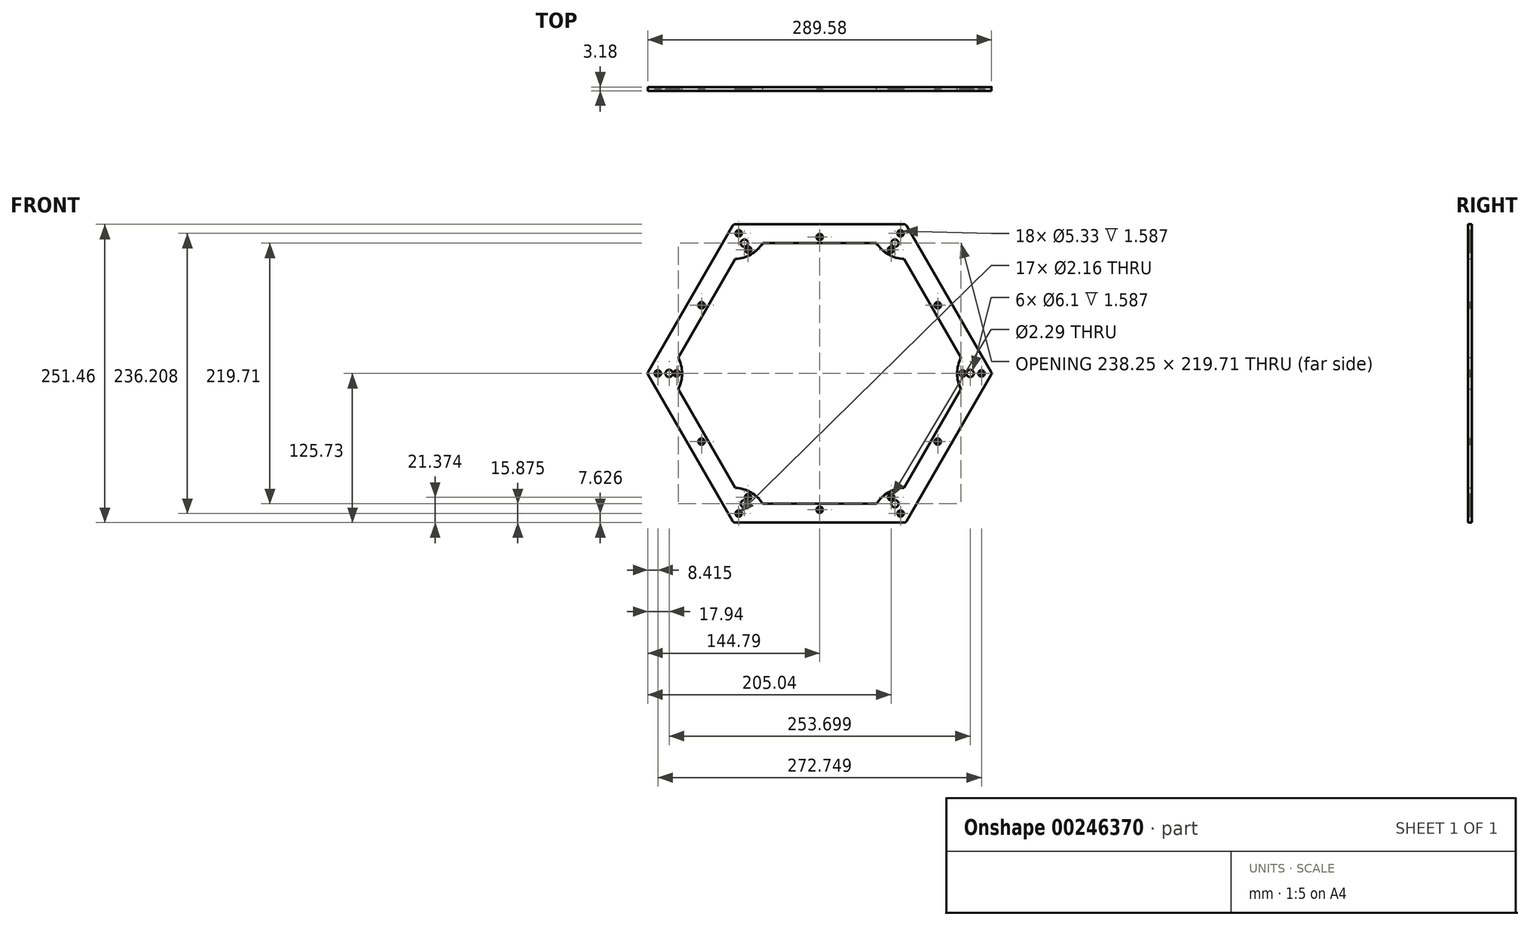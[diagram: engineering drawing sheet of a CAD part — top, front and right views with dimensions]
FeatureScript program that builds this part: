
annotation { "Feature Type Name" : "Feature", "Feature Type Description" : "" }
export const myFeature = defineFeature(function(context is Context, id is Id, definition is map)
    precondition{}
    {
        {
            var Q0;
            Q0=qCreatedBy(makeId("Front.planeOp"),FACE);
            var sketch = newSketch(context, id + "F0", { "sketchPlane" : qUnion([Q0])});
            skCircle(sketch, "E0.cCircle", {"center": v(0, 0) * mm, "radius": 125.73 * mm, "construction": true});
            skLineSegment(sketch, "E0.0", {"start": v(-72.6, 125.73) * mm, "end": v(72.6, 125.73) * mm});
            skLineSegment(sketch, "E0.1", {"start": v(72.6, 125.73) * mm, "end": v(145.18, 0) * mm});
            skLineSegment(sketch, "E0.2", {"start": v(145.18, 0) * mm, "end": v(72.6, -125.73) * mm});
            skLineSegment(sketch, "E0.3", {"start": v(72.6, -125.73) * mm, "end": v(-72.6, -125.73) * mm});
            skLineSegment(sketch, "E0.4", {"start": v(-72.6, -125.73) * mm, "end": v(-145.18, 0) * mm});
            skLineSegment(sketch, "E0.5", {"start": v(-145.18, 0) * mm, "end": v(-72.6, 125.73) * mm});
            skPoint(sketch, "E0.0.midPoint", {"position": v(0, 125.73) * mm});
            skLineSegment(sketch, "E1", {"start": v(0, 0) * mm, "end": v(-103.66, 179.55) * mm, "construction": true});
            skLineSegment(sketch, "E2", {"start": v(0, 0) * mm, "end": v(108.03, 187.1) * mm, "construction": true});
            skLineSegment(sketch, "E3", {"start": v(0, 0) * mm, "end": v(215.11, 0) * mm, "construction": true});
            skLineSegment(sketch, "E4", {"start": v(0, 0) * mm, "end": v(129.36, -224.05) * mm, "construction": true});
            skLineSegment(sketch, "E5", {"start": v(0, 0) * mm, "end": v(-137.05, -237.38) * mm, "construction": true});
            skLineSegment(sketch, "E6", {"start": v(0, 0) * mm, "end": v(-290.92, 0) * mm, "construction": true});
            skCircle(sketch, "E7.cCircle", {"center": v(0, 0) * mm, "radius": 109.86 * mm, "construction": true});
            skLineSegment(sketch, "E7.0", {"start": v(-63.42, 109.86) * mm, "end": v(63.42, 109.86) * mm});
            skLineSegment(sketch, "E7.1", {"start": v(63.42, 109.85) * mm, "end": v(126.85, 0) * mm});
            skLineSegment(sketch, "E7.2", {"start": v(126.85, 0) * mm, "end": v(63.42, -109.86) * mm});
            skLineSegment(sketch, "E7.3", {"start": v(63.42, -109.85) * mm, "end": v(-63.42, -109.86) * mm});
            skLineSegment(sketch, "E7.4", {"start": v(-63.42, -109.86) * mm, "end": v(-126.85, 0) * mm});
            skLineSegment(sketch, "E7.5", {"start": v(-126.85, 0) * mm, "end": v(-63.42, 109.86) * mm});
            skPoint(sketch, "E7.0.midPoint", {"position": v(0, 109.86) * mm});
            skCircle(sketch, "E8", {"center": v(-72.6, 125.73) * mm, "radius": 29.3 * mm});
            skCircle(sketch, "E9", {"center": v(72.6, 125.73) * mm, "radius": 29.3 * mm});
            skCircle(sketch, "E10", {"center": v(145.18, 0) * mm, "radius": 29.3 * mm});
            skCircle(sketch, "E11", {"center": v(72.6, -125.73) * mm, "radius": 29.3 * mm});
            skCircle(sketch, "E12", {"center": v(-72.6, -125.73) * mm, "radius": 29.3 * mm});
            skCircle(sketch, "E13", {"center": v(-145.18, 0) * mm, "radius": 29.3 * mm});
            skCircle(sketch, "E14", {"center": v(0, 0) * mm, "radius": 115.89 * mm, "construction": true});
            skSolve(sketch);
        }
        {
            var Q0;
            {var subQ0=sQuery(id+"F0.wireOp",EDGE,"E8");var subQ1=sQuery(id+"F0.wireOp",EDGE,"E0.0");var subQ2=makeQuery(id+"F0.imprint","INTERSECT",VERTEX,{"derivedFrom":[subQ1,subQ0]});Q0=makeQuery(id+"F0.imprint","IMPRINT",FACE,{"disambiguationData":[TD([[makeQuery(id+"F0.imprint","IMPRINT",EDGE,{"disambiguationData":[TD([[subQ2,-1.0]])],"derivedFrom":subQ1}),-1.0]])]});}
            var Q1;
            {var subQ6=sQuery(id+"F0.wireOp",EDGE,"E0.0");var subQ8=sQuery(id+"F0.wireOp",EDGE,"E0.5");var subQ9=makeQuery(id+"F0.imprint","INTERSECT",VERTEX,{"derivedFrom":[subQ6,subQ8]});Q1=makeQuery(id+"F0.imprint","IMPRINT",FACE,{"disambiguationData":[TD([[makeQuery(id+"F0.imprint","IMPRINT",EDGE,{"disambiguationData":[TD([[subQ9,-1.0]])],"derivedFrom":subQ6}),-1.0]])]});}
            var Q2;
            {var subQ0=sQuery(id+"F0.wireOp",EDGE,"E13");var subQ1=sQuery(id+"F0.wireOp",EDGE,"E0.5");var subQ2=makeQuery(id+"F0.imprint","INTERSECT",VERTEX,{"derivedFrom":[subQ1,subQ0]});Q2=makeQuery(id+"F0.imprint","IMPRINT",FACE,{"disambiguationData":[TD([[makeQuery(id+"F0.imprint","IMPRINT",EDGE,{"disambiguationData":[TD([[subQ2,-1.0]])],"derivedFrom":subQ1}),-1.0]])]});}
            var Q3;
            {var subQ6=sQuery(id+"F0.wireOp",EDGE,"E0.5");var subQ7=sQuery(id+"F0.wireOp",EDGE,"E0.4");var subQ8=makeQuery(id+"F0.imprint","INTERSECT",VERTEX,{"derivedFrom":[subQ7,subQ6]});Q3=makeQuery(id+"F0.imprint","IMPRINT",FACE,{"disambiguationData":[TD([[makeQuery(id+"F0.imprint","IMPRINT",EDGE,{"disambiguationData":[TD([[subQ8,1.0]])],"derivedFrom":subQ7}),-1.0]])]});}
            var Q4;
            {var subQ0=sQuery(id+"F0.wireOp",EDGE,"E7.5");var subQ1=sQuery(id+"F0.wireOp",EDGE,"E7.4");var subQ2=makeQuery(id+"F0.imprint","INTERSECT",VERTEX,{"derivedFrom":[subQ1,subQ0]});Q4=makeQuery(id+"F0.imprint","IMPRINT",FACE,{"disambiguationData":[TD([[makeQuery(id+"F0.imprint","IMPRINT",EDGE,{"disambiguationData":[TD([[subQ2,1.0]])],"derivedFrom":subQ1}),-1.0]])]});}
            var Q5;
            {var subQ0=sQuery(id+"F0.wireOp",EDGE,"E7.5");var subQ1=sQuery(id+"F0.wireOp",EDGE,"E7.0");var subQ2=makeQuery(id+"F0.imprint","INTERSECT",VERTEX,{"derivedFrom":[subQ1,subQ0]});Q5=makeQuery(id+"F0.imprint","IMPRINT",FACE,{"disambiguationData":[TD([[makeQuery(id+"F0.imprint","IMPRINT",EDGE,{"disambiguationData":[TD([[subQ2,-1.0]])],"derivedFrom":subQ1}),-1.0]])]});}
            var Q6;
            {var subQ0=sQuery(id+"F0.wireOp",EDGE,"E7.1");var subQ1=sQuery(id+"F0.wireOp",EDGE,"E7.0");var subQ2=makeQuery(id+"F0.imprint","INTERSECT",VERTEX,{"derivedFrom":[subQ1,subQ0]});Q6=makeQuery(id+"F0.imprint","IMPRINT",FACE,{"disambiguationData":[TD([[makeQuery(id+"F0.imprint","IMPRINT",EDGE,{"disambiguationData":[TD([[subQ2,1.0]])],"derivedFrom":subQ1}),-1.0]])]});}
            var Q7;
            {var subQ6=sQuery(id+"F0.wireOp",EDGE,"E0.1");var subQ7=sQuery(id+"F0.wireOp",EDGE,"E0.0");var subQ8=makeQuery(id+"F0.imprint","INTERSECT",VERTEX,{"derivedFrom":[subQ7,subQ6]});Q7=makeQuery(id+"F0.imprint","IMPRINT",FACE,{"disambiguationData":[TD([[makeQuery(id+"F0.imprint","IMPRINT",EDGE,{"disambiguationData":[TD([[subQ8,1.0]])],"derivedFrom":subQ7}),-1.0]])]});}
            var Q8;
            {var subQ0=sQuery(id+"F0.wireOp",EDGE,"E9");var subQ1=sQuery(id+"F0.wireOp",EDGE,"E0.1");var subQ2=makeQuery(id+"F0.imprint","INTERSECT",VERTEX,{"derivedFrom":[subQ1,subQ0]});Q8=makeQuery(id+"F0.imprint","IMPRINT",FACE,{"disambiguationData":[TD([[makeQuery(id+"F0.imprint","IMPRINT",EDGE,{"disambiguationData":[TD([[subQ2,-1.0]])],"derivedFrom":subQ1}),-1.0]])]});}
            var Q9;
            {var subQ0=sQuery(id+"F0.wireOp",EDGE,"E7.2");var subQ1=sQuery(id+"F0.wireOp",EDGE,"E7.1");var subQ2=makeQuery(id+"F0.imprint","INTERSECT",VERTEX,{"derivedFrom":[subQ1,subQ0]});Q9=makeQuery(id+"F0.imprint","IMPRINT",FACE,{"disambiguationData":[TD([[makeQuery(id+"F0.imprint","IMPRINT",EDGE,{"disambiguationData":[TD([[subQ2,1.0]])],"derivedFrom":subQ1}),-1.0]])]});}
            var Q10;
            {var subQ5=sQuery(id+"F0.wireOp",EDGE,"E0.2");var subQ6=sQuery(id+"F0.wireOp",EDGE,"E0.1");var subQ7=makeQuery(id+"F0.imprint","INTERSECT",VERTEX,{"derivedFrom":[subQ6,subQ5]});Q10=makeQuery(id+"F0.imprint","IMPRINT",FACE,{"disambiguationData":[TD([[makeQuery(id+"F0.imprint","IMPRINT",EDGE,{"disambiguationData":[TD([[subQ7,1.0]])],"derivedFrom":subQ6}),-1.0]])]});}
            var Q11;
            {var subQ0=sQuery(id+"F0.wireOp",EDGE,"E10");var subQ1=sQuery(id+"F0.wireOp",EDGE,"E0.2");var subQ2=makeQuery(id+"F0.imprint","INTERSECT",VERTEX,{"derivedFrom":[subQ1,subQ0]});Q11=makeQuery(id+"F0.imprint","IMPRINT",FACE,{"disambiguationData":[TD([[makeQuery(id+"F0.imprint","IMPRINT",EDGE,{"disambiguationData":[TD([[subQ2,-1.0]])],"derivedFrom":subQ1}),-1.0]])]});}
            var Q12;
            {var subQ6=sQuery(id+"F0.wireOp",EDGE,"E0.3");var subQ7=sQuery(id+"F0.wireOp",EDGE,"E0.2");var subQ8=makeQuery(id+"F0.imprint","INTERSECT",VERTEX,{"derivedFrom":[subQ7,subQ6]});Q12=makeQuery(id+"F0.imprint","IMPRINT",FACE,{"disambiguationData":[TD([[makeQuery(id+"F0.imprint","IMPRINT",EDGE,{"disambiguationData":[TD([[subQ8,1.0]])],"derivedFrom":subQ7}),-1.0]])]});}
            var Q13;
            {var subQ0=sQuery(id+"F0.wireOp",EDGE,"E7.3");var subQ1=sQuery(id+"F0.wireOp",EDGE,"E7.2");var subQ2=makeQuery(id+"F0.imprint","INTERSECT",VERTEX,{"derivedFrom":[subQ1,subQ0]});Q13=makeQuery(id+"F0.imprint","IMPRINT",FACE,{"disambiguationData":[TD([[makeQuery(id+"F0.imprint","IMPRINT",EDGE,{"disambiguationData":[TD([[subQ2,1.0]])],"derivedFrom":subQ1}),-1.0]])]});}
            var Q14;
            {var subQ0=sQuery(id+"F0.wireOp",EDGE,"E11");var subQ1=sQuery(id+"F0.wireOp",EDGE,"E0.3");var subQ2=makeQuery(id+"F0.imprint","INTERSECT",VERTEX,{"derivedFrom":[subQ1,subQ0]});Q14=makeQuery(id+"F0.imprint","IMPRINT",FACE,{"disambiguationData":[TD([[makeQuery(id+"F0.imprint","IMPRINT",EDGE,{"disambiguationData":[TD([[subQ2,-1.0]])],"derivedFrom":subQ1}),-1.0]])]});}
            var Q15;
            {var subQ6=sQuery(id+"F0.wireOp",EDGE,"E0.4");var subQ8=sQuery(id+"F0.wireOp",EDGE,"E0.3");var subQ9=makeQuery(id+"F0.imprint","INTERSECT",VERTEX,{"derivedFrom":[subQ8,subQ6]});Q15=makeQuery(id+"F0.imprint","IMPRINT",FACE,{"disambiguationData":[TD([[makeQuery(id+"F0.imprint","IMPRINT",EDGE,{"disambiguationData":[TD([[subQ9,1.0]])],"derivedFrom":subQ8}),-1.0]])]});}
            var Q16;
            {var subQ0=sQuery(id+"F0.wireOp",EDGE,"E7.4");var subQ1=sQuery(id+"F0.wireOp",EDGE,"E7.3");var subQ2=makeQuery(id+"F0.imprint","INTERSECT",VERTEX,{"derivedFrom":[subQ1,subQ0]});Q16=makeQuery(id+"F0.imprint","IMPRINT",FACE,{"disambiguationData":[TD([[makeQuery(id+"F0.imprint","IMPRINT",EDGE,{"disambiguationData":[TD([[subQ2,1.0]])],"derivedFrom":subQ1}),-1.0]])]});}
            var Q17;
            {var subQ0=sQuery(id+"F0.wireOp",EDGE,"E12");var subQ1=sQuery(id+"F0.wireOp",EDGE,"E0.4");var subQ2=makeQuery(id+"F0.imprint","INTERSECT",VERTEX,{"derivedFrom":[subQ1,subQ0]});Q17=makeQuery(id+"F0.imprint","IMPRINT",FACE,{"disambiguationData":[TD([[makeQuery(id+"F0.imprint","IMPRINT",EDGE,{"disambiguationData":[TD([[subQ2,-1.0]])],"derivedFrom":subQ1}),-1.0]])]});}
            extrude(context, id + "F1", {"entities" : qUnion([Q0, Q1, Q2, Q3, Q4, Q5, Q6, Q7, Q8, Q9, Q10, Q11, Q12, Q13, Q14, Q15, Q16, Q17]), "depth" : 3.17 * mm});
        }
        {
            var Q0;
            Q0=makeQuery(id+"F1.opExtrude","CAP_FACE",FACE,{"disambiguationData":[OSD([sQuery(id+"F0.wireOp",EDGE,"E0.0"),sQuery(id+"F0.wireOp",EDGE,"E0.1"),sQuery(id+"F0.wireOp",EDGE,"E0.2"),sQuery(id+"F0.wireOp",EDGE,"E0.3"),sQuery(id+"F0.wireOp",EDGE,"E0.4"),sQuery(id+"F0.wireOp",EDGE,"E0.5"),sQuery(id+"F0.wireOp",EDGE,"E7.0"),sQuery(id+"F0.wireOp",EDGE,"E7.1"),sQuery(id+"F0.wireOp",EDGE,"E7.2"),sQuery(id+"F0.wireOp",EDGE,"E7.3"),sQuery(id+"F0.wireOp",EDGE,"E7.4"),sQuery(id+"F0.wireOp",EDGE,"E7.5"),sQuery(id+"F0.wireOp",EDGE,"E8"),sQuery(id+"F0.wireOp",EDGE,"E9"),sQuery(id+"F0.wireOp",EDGE,"E10"),sQuery(id+"F0.wireOp",EDGE,"E11"),sQuery(id+"F0.wireOp",EDGE,"E12"),sQuery(id+"F0.wireOp",EDGE,"E13")])],"isStart":false});
            var sketch = newSketch(context, id + "F2", { "sketchPlane" : qUnion([Q0])});
            skCircle(sketch, "E15", {"center": v(-63.42, 109.86) * mm, "radius": 3.05 * mm});
            skCircle(sketch, "E16", {"center": v(63.42, 109.86) * mm, "radius": 3.05 * mm});
            skCircle(sketch, "E17", {"center": v(-126.85, 0) * mm, "radius": 3.05 * mm});
            skCircle(sketch, "E18", {"center": v(-63.42, -109.86) * mm, "radius": 3.05 * mm});
            skCircle(sketch, "E19", {"center": v(63.42, -109.85) * mm, "radius": 3.05 * mm});
            skCircle(sketch, "E20", {"center": v(126.85, 0) * mm, "radius": 3.05 * mm});
            skSolve(sketch);
        }
        {
            var Q0;
            Q0=qSketchRegion(id+"F2",true);
            extrude(context, id + "F3", {"entities" : qUnion([Q0]), "operationType" : NewBodyOperationType.REMOVE, "oppositeDirection" : true, "depth" : 1.59 * mm});
        }
        {
            var Q0;
            Q0=makeQuery(id+"F1.opExtrude","CAP_FACE",FACE,{"disambiguationData":[OSD([sQuery(id+"F0.wireOp",EDGE,"E0.0"),sQuery(id+"F0.wireOp",EDGE,"E0.1"),sQuery(id+"F0.wireOp",EDGE,"E0.2"),sQuery(id+"F0.wireOp",EDGE,"E0.3"),sQuery(id+"F0.wireOp",EDGE,"E0.4"),sQuery(id+"F0.wireOp",EDGE,"E0.5"),sQuery(id+"F0.wireOp",EDGE,"E7.0"),sQuery(id+"F0.wireOp",EDGE,"E7.1"),sQuery(id+"F0.wireOp",EDGE,"E7.2"),sQuery(id+"F0.wireOp",EDGE,"E7.3"),sQuery(id+"F0.wireOp",EDGE,"E7.4"),sQuery(id+"F0.wireOp",EDGE,"E7.5"),sQuery(id+"F0.wireOp",EDGE,"E8"),sQuery(id+"F0.wireOp",EDGE,"E9"),sQuery(id+"F0.wireOp",EDGE,"E10"),sQuery(id+"F0.wireOp",EDGE,"E11"),sQuery(id+"F0.wireOp",EDGE,"E12"),sQuery(id+"F0.wireOp",EDGE,"E13")])],"isStart":false});
            var sketch = newSketch(context, id + "F4", { "sketchPlane" : qUnion([Q0])});
            skCircle(sketch, "E21", {"center": v(-60.25, 104.36) * mm, "radius": 1.08 * mm});
            skLineSegment(sketch, "E22", {"start": v(-63.42, 109.86) * mm, "end": v(-60.25, 104.36) * mm, "construction": true});
            skLineSegment(sketch, "E23", {"start": v(63.42, 109.86) * mm, "end": v(60.25, 104.36) * mm, "construction": true});
            skLineSegment(sketch, "E24", {"start": v(126.85, 0) * mm, "end": v(120.5, 0) * mm, "construction": true});
            skLineSegment(sketch, "E25", {"start": v(63.42, -109.86) * mm, "end": v(60.25, -104.36) * mm, "construction": true});
            skLineSegment(sketch, "E26", {"start": v(-63.42, -109.86) * mm, "end": v(-60.25, -104.36) * mm, "construction": true});
            skLineSegment(sketch, "E27", {"start": v(-126.85, 0) * mm, "end": v(-120.5, 0) * mm, "construction": true});
            skCircle(sketch, "E28", {"center": v(60.25, 104.36) * mm, "radius": 1.08 * mm});
            skCircle(sketch, "E29", {"center": v(120.5, 0) * mm, "radius": 1.08 * mm});
            skCircle(sketch, "E30", {"center": v(60.25, -104.36) * mm, "radius": 1.14 * mm});
            skCircle(sketch, "E31", {"center": v(-60.25, -104.36) * mm, "radius": 1.08 * mm});
            skCircle(sketch, "E32", {"center": v(-120.5, 0) * mm, "radius": 1.08 * mm});
            skCircle(sketch, "E33", {"center": v(-120.5, 0) * mm, "radius": 2.67 * mm});
            skCircle(sketch, "E34", {"center": v(-60.25, 104.36) * mm, "radius": 2.67 * mm});
            skCircle(sketch, "E35", {"center": v(60.25, 104.36) * mm, "radius": 2.67 * mm});
            skCircle(sketch, "E36", {"center": v(120.5, 0) * mm, "radius": 2.67 * mm});
            skCircle(sketch, "E37", {"center": v(60.25, -104.36) * mm, "radius": 2.67 * mm});
            skCircle(sketch, "E38", {"center": v(-60.25, -104.36) * mm, "radius": 2.67 * mm});
            skCircle(sketch, "E39", {"center": v(-68.19, 118.1) * mm, "radius": 2.67 * mm});
            skLineSegment(sketch, "E40", {"start": v(-63.42, 109.86) * mm, "end": v(-68.19, 118.1) * mm, "construction": true});
            skCircle(sketch, "E41", {"center": v(-68.19, 118.1) * mm, "radius": 1.08 * mm});
            skLineSegment(sketch, "E42", {"start": v(63.42, 109.86) * mm, "end": v(68.19, 118.1) * mm, "construction": true});
            skCircle(sketch, "E43", {"center": v(68.19, 118.1) * mm, "radius": 2.67 * mm});
            skCircle(sketch, "E44", {"center": v(68.19, 118.1) * mm, "radius": 1.08 * mm});
            skLineSegment(sketch, "E45", {"start": v(-126.85, 0) * mm, "end": v(-136.37, 0) * mm, "construction": true});
            skCircle(sketch, "E46", {"center": v(-136.37, 0) * mm, "radius": 2.67 * mm});
            skCircle(sketch, "E47", {"center": v(-136.37, 0) * mm, "radius": 1.08 * mm});
            skLineSegment(sketch, "E48", {"start": v(-63.42, -109.86) * mm, "end": v(-68.19, -118.1) * mm, "construction": true});
            skCircle(sketch, "E49", {"center": v(-68.19, -118.1) * mm, "radius": 2.67 * mm});
            skCircle(sketch, "E50", {"center": v(-68.19, -118.1) * mm, "radius": 1.08 * mm});
            skLineSegment(sketch, "E51", {"start": v(126.85, 0) * mm, "end": v(136.37, 0) * mm, "construction": true});
            skCircle(sketch, "E52", {"center": v(136.37, 0) * mm, "radius": 2.67 * mm});
            skCircle(sketch, "E53", {"center": v(136.37, 0) * mm, "radius": 1.08 * mm});
            skLineSegment(sketch, "E54", {"start": v(63.42, -109.86) * mm, "end": v(68.19, -118.1) * mm, "construction": true});
            skCircle(sketch, "E55", {"center": v(68.19, -118.1) * mm, "radius": 2.67 * mm});
            skCircle(sketch, "E56", {"center": v(68.19, -118.1) * mm, "radius": 1.08 * mm});
            skCircle(sketch, "E57", {"center": v(0, 114.94) * mm, "radius": 2.67 * mm});
            skCircle(sketch, "E58", {"center": v(0, 114.94) * mm, "radius": 1.08 * mm});
            skCircle(sketch, "E59.1.0", {"center": v(-99.54, 57.47) * mm, "radius": 1.08 * mm});
            skCircle(sketch, "E59.1.1", {"center": v(-99.54, 57.47) * mm, "radius": 2.67 * mm});
            skCircle(sketch, "E59.2.0", {"center": v(-99.54, -57.47) * mm, "radius": 1.08 * mm});
            skCircle(sketch, "E59.2.1", {"center": v(-99.54, -57.47) * mm, "radius": 2.67 * mm});
            skCircle(sketch, "E59.3.0", {"center": v(0, -114.94) * mm, "radius": 1.08 * mm});
            skCircle(sketch, "E59.3.1", {"center": v(0, -114.94) * mm, "radius": 2.67 * mm});
            skCircle(sketch, "E59.4.0", {"center": v(99.54, -57.47) * mm, "radius": 1.08 * mm});
            skCircle(sketch, "E59.4.1", {"center": v(99.54, -57.47) * mm, "radius": 2.67 * mm});
            skCircle(sketch, "E59.5.0", {"center": v(99.54, 57.47) * mm, "radius": 1.08 * mm});
            skCircle(sketch, "E59.5.1", {"center": v(99.54, 57.47) * mm, "radius": 2.67 * mm});
            skPoint(sketch, "E59.center", {"position": v(0, 0) * mm});
            skLineSegment(sketch, "E60", {"start": v(0, 0) * mm, "end": v(99.54, 57.47) * mm, "construction": true});
            skLineSegment(sketch, "E61", {"start": v(0, 0) * mm, "end": v(0, -114.94) * mm, "construction": true});
            skLineSegment(sketch, "E62", {"start": v(0, 0) * mm, "end": v(99.54, -57.47) * mm, "construction": true});
            skLineSegment(sketch, "E63", {"start": v(0, 0) * mm, "end": v(-99.54, -57.47) * mm, "construction": true});
            skLineSegment(sketch, "E64", {"start": v(0, 0) * mm, "end": v(0, 114.94) * mm, "construction": true});
            skLineSegment(sketch, "E65", {"start": v(0, 0) * mm, "end": v(-99.54, 57.47) * mm, "construction": true});
            skSolve(sketch);
        }
        {
            var Q0;
            Q0=makeQuery(id+"F4.imprint","IMPRINT",FACE,{"disambiguationData":[TD([[makeQuery(id+"F4.imprint","IMPRINT",EDGE,{"derivedFrom":sQuery(id+"F4.wireOp",EDGE,"E32")}),-1.0]])]});
            var Q1;
            Q1=makeQuery(id+"F4.imprint","IMPRINT",FACE,{"disambiguationData":[TD([[makeQuery(id+"F4.imprint","IMPRINT",EDGE,{"derivedFrom":sQuery(id+"F4.wireOp",EDGE,"E21")}),-1.0]])]});
            var Q2;
            Q2=makeQuery(id+"F4.imprint","IMPRINT",FACE,{"disambiguationData":[TD([[makeQuery(id+"F4.imprint","IMPRINT",EDGE,{"derivedFrom":sQuery(id+"F4.wireOp",EDGE,"E28")}),-1.0]])]});
            var Q3;
            Q3=makeQuery(id+"F4.imprint","IMPRINT",FACE,{"disambiguationData":[TD([[makeQuery(id+"F4.imprint","IMPRINT",EDGE,{"derivedFrom":sQuery(id+"F4.wireOp",EDGE,"E29")}),-1.0]])]});
            var Q4;
            Q4=makeQuery(id+"F4.imprint","IMPRINT",FACE,{"disambiguationData":[TD([[makeQuery(id+"F4.imprint","IMPRINT",EDGE,{"derivedFrom":sQuery(id+"F4.wireOp",EDGE,"E30")}),-1.0]])]});
            var Q5;
            Q5=makeQuery(id+"F4.imprint","IMPRINT",FACE,{"disambiguationData":[TD([[makeQuery(id+"F4.imprint","IMPRINT",EDGE,{"derivedFrom":sQuery(id+"F4.wireOp",EDGE,"E31")}),-1.0]])]});
            var Q6;
            Q6=makeQuery(id+"F4.imprint","IMPRINT",FACE,{"disambiguationData":[TD([[makeQuery(id+"F4.imprint","IMPRINT",EDGE,{"derivedFrom":sQuery(id+"F4.wireOp",EDGE,"E49")}),1.0]])]});
            var Q7;
            Q7=makeQuery(id+"F4.imprint","IMPRINT",FACE,{"disambiguationData":[TD([[makeQuery(id+"F4.imprint","IMPRINT",EDGE,{"derivedFrom":sQuery(id+"F4.wireOp",EDGE,"E55")}),1.0]])]});
            var Q8;
            Q8=makeQuery(id+"F4.imprint","IMPRINT",FACE,{"disambiguationData":[TD([[makeQuery(id+"F4.imprint","IMPRINT",EDGE,{"derivedFrom":sQuery(id+"F4.wireOp",EDGE,"E52")}),1.0]])]});
            var Q9;
            Q9=makeQuery(id+"F4.imprint","IMPRINT",FACE,{"disambiguationData":[TD([[makeQuery(id+"F4.imprint","IMPRINT",EDGE,{"derivedFrom":sQuery(id+"F4.wireOp",EDGE,"E43")}),1.0]])]});
            var Q10;
            Q10=makeQuery(id+"F4.imprint","IMPRINT",FACE,{"disambiguationData":[TD([[makeQuery(id+"F4.imprint","IMPRINT",EDGE,{"derivedFrom":sQuery(id+"F4.wireOp",EDGE,"E39")}),1.0]])]});
            var Q11;
            Q11=makeQuery(id+"F4.imprint","IMPRINT",FACE,{"disambiguationData":[TD([[makeQuery(id+"F4.imprint","IMPRINT",EDGE,{"derivedFrom":sQuery(id+"F4.wireOp",EDGE,"E46")}),1.0]])]});
            var Q12;
            Q12=makeQuery(id+"F4.imprint","IMPRINT",FACE,{"disambiguationData":[TD([[makeQuery(id+"F4.imprint","IMPRINT",EDGE,{"derivedFrom":sQuery(id+"F4.wireOp",EDGE,"E59.1.0")}),-1.0]])]});
            var Q13;
            Q13=makeQuery(id+"F4.imprint","IMPRINT",FACE,{"disambiguationData":[TD([[makeQuery(id+"F4.imprint","IMPRINT",EDGE,{"derivedFrom":sQuery(id+"F4.wireOp",EDGE,"E57")}),1.0]])]});
            var Q14;
            Q14=makeQuery(id+"F4.imprint","IMPRINT",FACE,{"disambiguationData":[TD([[makeQuery(id+"F4.imprint","IMPRINT",EDGE,{"derivedFrom":sQuery(id+"F4.wireOp",EDGE,"E59.5.0")}),-1.0]])]});
            var Q15;
            Q15=makeQuery(id+"F4.imprint","IMPRINT",FACE,{"disambiguationData":[TD([[makeQuery(id+"F4.imprint","IMPRINT",EDGE,{"derivedFrom":sQuery(id+"F4.wireOp",EDGE,"E59.4.0")}),-1.0]])]});
            var Q16;
            Q16=makeQuery(id+"F4.imprint","IMPRINT",FACE,{"disambiguationData":[TD([[makeQuery(id+"F4.imprint","IMPRINT",EDGE,{"derivedFrom":sQuery(id+"F4.wireOp",EDGE,"E59.3.0")}),-1.0]])]});
            var Q17;
            Q17=makeQuery(id+"F4.imprint","IMPRINT",FACE,{"disambiguationData":[TD([[makeQuery(id+"F4.imprint","IMPRINT",EDGE,{"derivedFrom":sQuery(id+"F4.wireOp",EDGE,"E59.2.0")}),-1.0]])]});
            extrude(context, id + "F5", {"entities" : qUnion([Q0, Q1, Q2, Q3, Q4, Q5, Q6, Q7, Q8, Q9, Q10, Q11, Q12, Q13, Q14, Q15, Q16, Q17]), "operationType" : NewBodyOperationType.REMOVE, "oppositeDirection" : true, "depth" : 1.59 * mm});
        }
        {
            var Q0;
            Q0=makeQuery(id+"F4.imprint","IMPRINT",FACE,{"disambiguationData":[TD([[makeQuery(id+"F4.imprint","IMPRINT",EDGE,{"derivedFrom":sQuery(id+"F4.wireOp",EDGE,"E31")}),1.0]])]});
            var Q1;
            Q1=makeQuery(id+"F4.imprint","IMPRINT",FACE,{"disambiguationData":[TD([[makeQuery(id+"F4.imprint","IMPRINT",EDGE,{"derivedFrom":sQuery(id+"F4.wireOp",EDGE,"E32")}),1.0]])]});
            var Q2;
            Q2=makeQuery(id+"F4.imprint","IMPRINT",FACE,{"disambiguationData":[TD([[makeQuery(id+"F4.imprint","IMPRINT",EDGE,{"derivedFrom":sQuery(id+"F4.wireOp",EDGE,"E21")}),1.0]])]});
            var Q3;
            Q3=makeQuery(id+"F4.imprint","IMPRINT",FACE,{"disambiguationData":[TD([[makeQuery(id+"F4.imprint","IMPRINT",EDGE,{"derivedFrom":sQuery(id+"F4.wireOp",EDGE,"E28")}),1.0]])]});
            var Q4;
            Q4=makeQuery(id+"F4.imprint","IMPRINT",FACE,{"disambiguationData":[TD([[makeQuery(id+"F4.imprint","IMPRINT",EDGE,{"derivedFrom":sQuery(id+"F4.wireOp",EDGE,"E29")}),1.0]])]});
            var Q5;
            Q5=makeQuery(id+"F4.imprint","IMPRINT",FACE,{"disambiguationData":[TD([[makeQuery(id+"F4.imprint","IMPRINT",EDGE,{"derivedFrom":sQuery(id+"F4.wireOp",EDGE,"E30")}),1.0]])]});
            var Q6;
            Q6=makeQuery(id+"F4.imprint","IMPRINT",FACE,{"disambiguationData":[TD([[makeQuery(id+"F4.imprint","IMPRINT",EDGE,{"derivedFrom":sQuery(id+"F4.wireOp",EDGE,"E47")}),1.0]])]});
            var Q7;
            Q7=makeQuery(id+"F4.imprint","IMPRINT",FACE,{"disambiguationData":[TD([[makeQuery(id+"F4.imprint","IMPRINT",EDGE,{"derivedFrom":sQuery(id+"F4.wireOp",EDGE,"E50")}),1.0]])]});
            var Q8;
            Q8=makeQuery(id+"F4.imprint","IMPRINT",FACE,{"disambiguationData":[TD([[makeQuery(id+"F4.imprint","IMPRINT",EDGE,{"derivedFrom":sQuery(id+"F4.wireOp",EDGE,"E56")}),1.0]])]});
            var Q9;
            Q9=makeQuery(id+"F4.imprint","IMPRINT",FACE,{"disambiguationData":[TD([[makeQuery(id+"F4.imprint","IMPRINT",EDGE,{"derivedFrom":sQuery(id+"F4.wireOp",EDGE,"E53")}),1.0]])]});
            var Q10;
            Q10=makeQuery(id+"F4.imprint","IMPRINT",FACE,{"disambiguationData":[TD([[makeQuery(id+"F4.imprint","IMPRINT",EDGE,{"derivedFrom":sQuery(id+"F4.wireOp",EDGE,"E44")}),1.0]])]});
            var Q11;
            Q11=makeQuery(id+"F4.imprint","IMPRINT",FACE,{"disambiguationData":[TD([[makeQuery(id+"F4.imprint","IMPRINT",EDGE,{"derivedFrom":sQuery(id+"F4.wireOp",EDGE,"E41")}),1.0]])]});
            var Q12;
            Q12=makeQuery(id+"F4.imprint","IMPRINT",FACE,{"disambiguationData":[TD([[makeQuery(id+"F4.imprint","IMPRINT",EDGE,{"derivedFrom":sQuery(id+"F4.wireOp",EDGE,"E59.1.0")}),1.0]])]});
            var Q13;
            Q13=makeQuery(id+"F4.imprint","IMPRINT",FACE,{"disambiguationData":[TD([[makeQuery(id+"F4.imprint","IMPRINT",EDGE,{"derivedFrom":sQuery(id+"F4.wireOp",EDGE,"E59.2.0")}),1.0]])]});
            var Q14;
            Q14=makeQuery(id+"F4.imprint","IMPRINT",FACE,{"disambiguationData":[TD([[makeQuery(id+"F4.imprint","IMPRINT",EDGE,{"derivedFrom":sQuery(id+"F4.wireOp",EDGE,"E59.3.0")}),1.0]])]});
            var Q15;
            Q15=makeQuery(id+"F4.imprint","IMPRINT",FACE,{"disambiguationData":[TD([[makeQuery(id+"F4.imprint","IMPRINT",EDGE,{"derivedFrom":sQuery(id+"F4.wireOp",EDGE,"E59.4.0")}),1.0]])]});
            var Q16;
            Q16=makeQuery(id+"F4.imprint","IMPRINT",FACE,{"disambiguationData":[TD([[makeQuery(id+"F4.imprint","IMPRINT",EDGE,{"derivedFrom":sQuery(id+"F4.wireOp",EDGE,"E59.5.0")}),1.0]])]});
            var Q17;
            Q17=makeQuery(id+"F4.imprint","IMPRINT",FACE,{"disambiguationData":[TD([[makeQuery(id+"F4.imprint","IMPRINT",EDGE,{"derivedFrom":sQuery(id+"F4.wireOp",EDGE,"E58")}),1.0]])]});
            extrude(context, id + "F6", {"entities" : qUnion([Q0, Q1, Q2, Q3, Q4, Q5, Q6, Q7, Q8, Q9, Q10, Q11, Q12, Q13, Q14, Q15, Q16, Q17]), "operationType" : NewBodyOperationType.REMOVE, "endBound" : BoundingType.THROUGH_ALL, "oppositeDirection" : true, "depth" : 25.4 * mm});
        }
        {
            var Q0;
            Q0=makeQuery(id+"F1.opExtrude","SWEPT_EDGE",EDGE,{"disambiguationData":[OSD([sQuery(id+"F0.wireOp",EDGE,"E0.0"),sQuery(id+"F0.wireOp",EDGE,"E0.5")])]});
            var Q1;
            Q1=makeQuery(id+"F1.opExtrude","SWEPT_EDGE",EDGE,{"disambiguationData":[OSD([sQuery(id+"F0.wireOp",EDGE,"E0.0"),sQuery(id+"F0.wireOp",EDGE,"E0.1")])]});
            var Q2;
            Q2=makeQuery(id+"F1.opExtrude","SWEPT_EDGE",EDGE,{"disambiguationData":[OSD([sQuery(id+"F0.wireOp",EDGE,"E0.1"),sQuery(id+"F0.wireOp",EDGE,"E0.2")])]});
            var Q3;
            Q3=makeQuery(id+"F1.opExtrude","SWEPT_EDGE",EDGE,{"disambiguationData":[OSD([sQuery(id+"F0.wireOp",EDGE,"E0.2"),sQuery(id+"F0.wireOp",EDGE,"E0.3")])]});
            var Q4;
            Q4=makeQuery(id+"F1.opExtrude","SWEPT_EDGE",EDGE,{"disambiguationData":[OSD([sQuery(id+"F0.wireOp",EDGE,"E0.3"),sQuery(id+"F0.wireOp",EDGE,"E0.4")])]});
            var Q5;
            Q5=makeQuery(id+"F1.opExtrude","SWEPT_EDGE",EDGE,{"disambiguationData":[OSD([sQuery(id+"F0.wireOp",EDGE,"E0.4"),sQuery(id+"F0.wireOp",EDGE,"E0.5")])]});
            fillet(context, id + "F7", {"entities" : qUnion([Q0, Q1, Q2, Q3, Q4, Q5]), "radius" : 2.54 * mm, "tangentPropagation" : true, "allowEdgeOverflow" : false});
        }
    });
